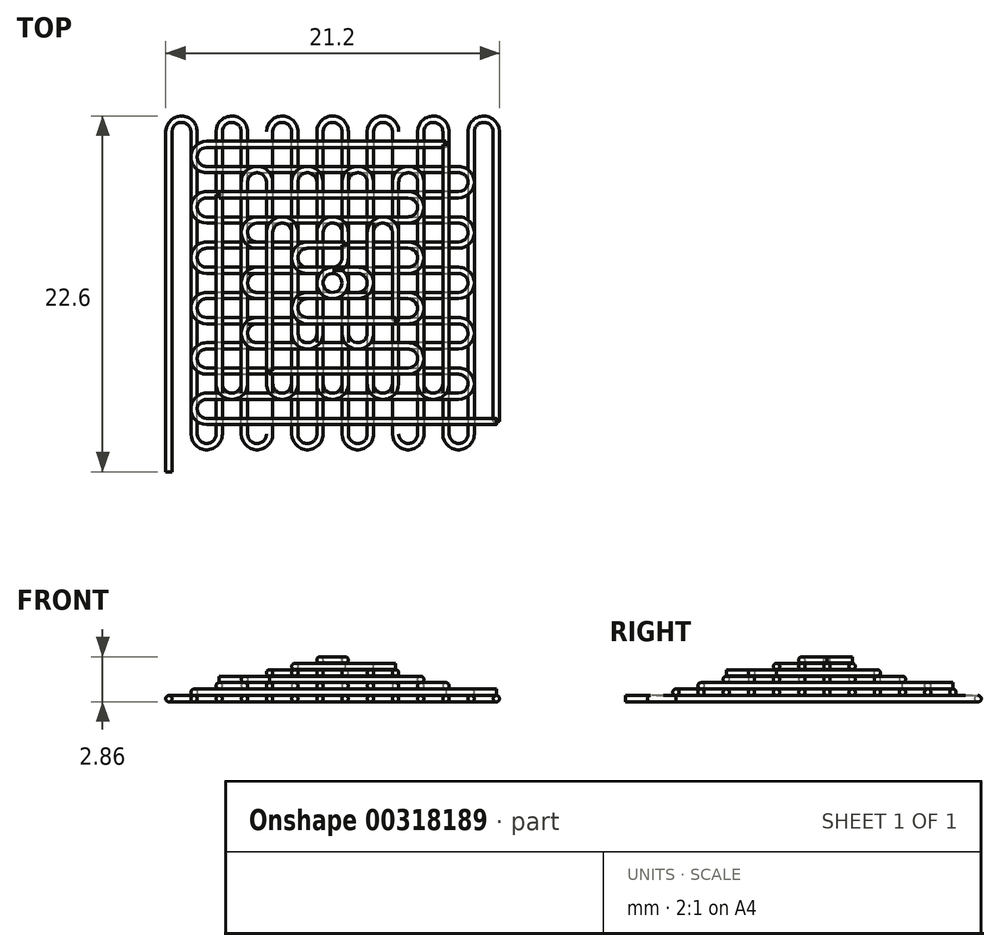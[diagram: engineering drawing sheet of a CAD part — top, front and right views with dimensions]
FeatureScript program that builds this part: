
annotation { "Feature Type Name" : "Feature", "Feature Type Description" : "" }
export const myFeature = defineFeature(function(context is Context, id is Id, definition is map)
    precondition{}
    {
        {
            var Q0;
            Q0=qCreatedBy(makeId("Top.planeOp"),FACE);
            cPlane(context, id + "F0", {"entities" : qUnion([Q0]), "cplaneType" : CPlaneType.OFFSET, "offset" : 0.2 * mm, "width" : 150 * mm, "height" : 150 * mm});
        }
        {
            var Q0;
            Q0=qCreatedBy(id+"F0.planeOp",FACE);
            var sketch = newSketch(context, id + "F1", { "sketchPlane" : qUnion([Q0])});
            skLineSegment(sketch, "E0.bottom", {"start": v(10.4, 10.4) * mm, "end": v(-10.4, 10.4) * mm});
            skLineSegment(sketch, "E0.top", {"start": v(10.4, -10.4) * mm, "end": v(-10.4, -10.4) * mm});
            skLineSegment(sketch, "E0.left", {"start": v(10.4, 10.4) * mm, "end": v(10.4, -10.4) * mm});
            skLineSegment(sketch, "E0.right", {"start": v(-10.4, 9.6) * mm, "end": v(-10.4, -10.4) * mm});
            skPoint(sketch, "E0.middle", {"position": v(0, 0) * mm});
            skLineSegment(sketch, "E1", {"start": v(-9.6, 10.4) * mm, "end": v(-9.6, 10.4) * mm});
            skLineSegment(sketch, "E2", {"start": v(-8.8, 9.6) * mm, "end": v(-8.8, -9.6) * mm});
            skLineSegment(sketch, "E3", {"start": v(-8.8, -10.4) * mm, "end": v(-10.4, -10.4) * mm});
            skLineSegment(sketch, "E4", {"start": v(-8.8, 10.4) * mm, "end": v(-7.2, 10.4) * mm});
            skLineSegment(sketch, "E5", {"start": v(-7.2, 10.4) * mm, "end": v(-7.2, -9.6) * mm});
            skLineSegment(sketch, "E6", {"start": v(-8, -10.4) * mm, "end": v(-8, -10.4) * mm});
            skPoint(sketch, "E7.visualSharp", {"position": v(-10.4, 10.4) * mm});
            skArc(sketch, "E7.filletArc", {"start": v(-9.6, 10.4) * mm, "mid": v(-10.17, 10.17) * mm, "end": v(-10.4, 9.6) * mm});
            skPoint(sketch, "E8.visualSharp", {"position": v(-8.8, 10.4) * mm});
            skArc(sketch, "E8.filletArc", {"start": v(-8.8, 9.6) * mm, "mid": v(-9.03, 10.17) * mm, "end": v(-9.6, 10.4) * mm});
            skPoint(sketch, "E9.visualSharp", {"position": v(-8.8, -10.4) * mm});
            skArc(sketch, "E9.filletArc", {"start": v(-8.8, -9.6) * mm, "mid": v(-8.57, -10.17) * mm, "end": v(-8, -10.4) * mm});
            skPoint(sketch, "E10.visualSharp", {"position": v(-7.2, -10.4) * mm});
            skArc(sketch, "E10.filletArc", {"start": v(-8, -10.4) * mm, "mid": v(-7.43, -10.17) * mm, "end": v(-7.2, -9.6) * mm});
            skLineSegment(sketch, "E11", {"start": v(-7.2, 9.6) * mm, "end": v(-7.2, -9.6) * mm});
            skArc(sketch, "E12.1.0.0", {"start": v(-6.4, 10.4) * mm, "mid": v(-6.97, 10.17) * mm, "end": v(-7.2, 9.6) * mm});
            skArc(sketch, "E12.1.0.1", {"start": v(-5.6, 9.6) * mm, "mid": v(-5.83, 10.17) * mm, "end": v(-6.4, 10.4) * mm});
            skLineSegment(sketch, "E12.1.0.2", {"start": v(-5.6, 9.6) * mm, "end": v(-5.6, -9.6) * mm});
            skArc(sketch, "E12.1.0.3", {"start": v(-5.6, -9.6) * mm, "mid": v(-5.37, -10.17) * mm, "end": v(-4.8, -10.4) * mm});
            skArc(sketch, "E12.1.0.4", {"start": v(-4.8, -10.4) * mm, "mid": v(-4.23, -10.17) * mm, "end": v(-4, -9.6) * mm});
            skLineSegment(sketch, "E12.1.0.5", {"start": v(-4, 9.6) * mm, "end": v(-4, -9.6) * mm});
            skArc(sketch, "E12.2.0.0", {"start": v(-3.2, 10.4) * mm, "mid": v(-3.77, 10.17) * mm, "end": v(-4, 9.6) * mm});
            skArc(sketch, "E12.2.0.1", {"start": v(-2.4, 9.6) * mm, "mid": v(-2.63, 10.17) * mm, "end": v(-3.2, 10.4) * mm});
            skLineSegment(sketch, "E12.2.0.2", {"start": v(-2.4, 9.6) * mm, "end": v(-2.4, -9.6) * mm});
            skArc(sketch, "E12.2.0.3", {"start": v(-2.4, -9.6) * mm, "mid": v(-2.17, -10.17) * mm, "end": v(-1.6, -10.4) * mm});
            skArc(sketch, "E12.2.0.4", {"start": v(-1.6, -10.4) * mm, "mid": v(-1.03, -10.17) * mm, "end": v(-0.8, -9.6) * mm});
            skLineSegment(sketch, "E12.2.0.5", {"start": v(-0.8, 9.6) * mm, "end": v(-0.8, -9.6) * mm});
            skArc(sketch, "E12.3.0.0", {"start": v(0, 10.4) * mm, "mid": v(-0.57, 10.17) * mm, "end": v(-0.8, 9.6) * mm});
            skArc(sketch, "E12.3.0.1", {"start": v(0.8, 9.6) * mm, "mid": v(0.57, 10.17) * mm, "end": v(0, 10.4) * mm});
            skLineSegment(sketch, "E12.3.0.2", {"start": v(0.8, 9.6) * mm, "end": v(0.8, -9.6) * mm});
            skArc(sketch, "E12.3.0.3", {"start": v(0.8, -9.6) * mm, "mid": v(1.03, -10.17) * mm, "end": v(1.6, -10.4) * mm});
            skArc(sketch, "E12.3.0.4", {"start": v(1.6, -10.4) * mm, "mid": v(2.17, -10.17) * mm, "end": v(2.4, -9.6) * mm});
            skLineSegment(sketch, "E12.3.0.5", {"start": v(2.4, 9.6) * mm, "end": v(2.4, -9.6) * mm});
            skArc(sketch, "E12.4.0.0", {"start": v(3.2, 10.4) * mm, "mid": v(2.63, 10.17) * mm, "end": v(2.4, 9.6) * mm});
            skArc(sketch, "E12.4.0.1", {"start": v(4, 9.6) * mm, "mid": v(3.77, 10.17) * mm, "end": v(3.2, 10.4) * mm});
            skLineSegment(sketch, "E12.4.0.2", {"start": v(4, 9.6) * mm, "end": v(4, -9.6) * mm});
            skArc(sketch, "E12.4.0.3", {"start": v(4, -9.6) * mm, "mid": v(4.23, -10.17) * mm, "end": v(4.8, -10.4) * mm});
            skArc(sketch, "E12.4.0.4", {"start": v(4.8, -10.4) * mm, "mid": v(5.37, -10.17) * mm, "end": v(5.6, -9.6) * mm});
            skLineSegment(sketch, "E12.4.0.5", {"start": v(5.6, 9.6) * mm, "end": v(5.6, -9.6) * mm});
            skArc(sketch, "E12.5.0.0", {"start": v(6.4, 10.4) * mm, "mid": v(5.83, 10.17) * mm, "end": v(5.6, 9.6) * mm});
            skArc(sketch, "E12.5.0.1", {"start": v(7.2, 9.6) * mm, "mid": v(6.97, 10.17) * mm, "end": v(6.4, 10.4) * mm});
            skLineSegment(sketch, "E12.5.0.2", {"start": v(7.2, 9.6) * mm, "end": v(7.2, -9.6) * mm});
            skArc(sketch, "E12.5.0.3", {"start": v(7.2, -9.6) * mm, "mid": v(7.43, -10.17) * mm, "end": v(8, -10.4) * mm});
            skArc(sketch, "E12.5.0.4", {"start": v(8, -10.4) * mm, "mid": v(8.57, -10.17) * mm, "end": v(8.8, -9.6) * mm});
            skLineSegment(sketch, "E12.5.0.5", {"start": v(8.8, 9.6) * mm, "end": v(8.8, -9.6) * mm});
            skLineSegment(sketch, "E12.direction1", {"start": v(-8, -10.4) * mm, "end": v(-4.8, -10.4) * mm, "construction": true});
            skLineSegment(sketch, "E13", {"start": v(10.4, 10.4) * mm, "end": v(10.4, 9.6) * mm});
            skArc(sketch, "E14", {"start": v(8.8, 9.6) * mm, "mid": v(9.6, 10.4) * mm, "end": v(10.4, 9.6) * mm});
            skLineSegment(sketch, "E15", {"start": v(-10.4, 9.6) * mm, "end": v(-10.4, -12) * mm});
            skLineSegment(sketch, "E16", {"start": v(10.4, -10.4) * mm, "end": v(10.4, -8.8) * mm});
            skLineSegment(sketch, "E17", {"start": v(10.4, -8.8) * mm, "end": v(10.4, 9.6) * mm});
            skSolve(sketch);
        }
        {
            var Q0;
            Q0=qCreatedBy(id+"F0.planeOp",FACE);
            cPlane(context, id + "F2", {"entities" : qUnion([Q0]), "cplaneType" : CPlaneType.OFFSET, "offset" : 0.4 * mm, "width" : 150 * mm, "height" : 150 * mm});
        }
        {
            var Q0;
            Q0=qCreatedBy(id+"F2.planeOp",FACE);
            var sketch = newSketch(context, id + "F3", { "sketchPlane" : qUnion([Q0])});
            skLineSegment(sketch, "E18.bottom", {"start": v(8.8, 8.8) * mm, "end": v(-8.8, 8.8) * mm});
            skLineSegment(sketch, "E18.top", {"start": v(8.8, -8.8) * mm, "end": v(-8, -8.8) * mm});
            skLineSegment(sketch, "E18.left", {"start": v(8.8, 8.8) * mm, "end": v(8.8, -8.8) * mm});
            skLineSegment(sketch, "E18.right", {"start": v(-8.8, 8.8) * mm, "end": v(-8.8, -8.8) * mm});
            skPoint(sketch, "E18.middle", {"position": v(0, 0) * mm});
            skLineSegment(sketch, "E19", {"start": v(-8.8, -8) * mm, "end": v(-8.8, -8) * mm});
            skLineSegment(sketch, "E20", {"start": v(-8, -7.2) * mm, "end": v(8, -7.2) * mm});
            skLineSegment(sketch, "E21", {"start": v(8.8, -7.2) * mm, "end": v(8.8, -8.8) * mm});
            skLineSegment(sketch, "E22", {"start": v(-8.8, -7.2) * mm, "end": v(-8.8, -5.6) * mm});
            skLineSegment(sketch, "E23", {"start": v(-8.8, -5.6) * mm, "end": v(8, -5.6) * mm});
            skLineSegment(sketch, "E24", {"start": v(8.8, -6.4) * mm, "end": v(8.8, -6.4) * mm});
            skPoint(sketch, "E25.visualSharp", {"position": v(-8.8, -8.8) * mm});
            skArc(sketch, "E25.filletArc", {"start": v(-8.8, -8) * mm, "mid": v(-8.57, -8.57) * mm, "end": v(-8, -8.8) * mm});
            skPoint(sketch, "E26.visualSharp", {"position": v(-8.8, -7.2) * mm});
            skArc(sketch, "E26.filletArc", {"start": v(-8, -7.2) * mm, "mid": v(-8.57, -7.43) * mm, "end": v(-8.8, -8) * mm});
            skPoint(sketch, "E27.visualSharp", {"position": v(8.8, -7.2) * mm});
            skArc(sketch, "E27.filletArc", {"start": v(8, -7.2) * mm, "mid": v(8.57, -6.97) * mm, "end": v(8.8, -6.4) * mm});
            skPoint(sketch, "E28.visualSharp", {"position": v(8.8, -5.6) * mm});
            skArc(sketch, "E28.filletArc", {"start": v(8.8, -6.4) * mm, "mid": v(8.57, -5.83) * mm, "end": v(8, -5.6) * mm});
            skLineSegment(sketch, "E29", {"start": v(-8, -5.6) * mm, "end": v(8, -5.6) * mm});
            skArc(sketch, "E30.1.0.0", {"start": v(-8.8, -4.8) * mm, "mid": v(-8.57, -5.37) * mm, "end": v(-8, -5.6) * mm});
            skArc(sketch, "E30.1.0.1", {"start": v(-8, -4) * mm, "mid": v(-8.57, -4.23) * mm, "end": v(-8.8, -4.8) * mm});
            skLineSegment(sketch, "E30.1.0.2", {"start": v(-8, -4) * mm, "end": v(8, -4) * mm});
            skArc(sketch, "E30.1.0.3", {"start": v(8, -4) * mm, "mid": v(8.57, -3.77) * mm, "end": v(8.8, -3.2) * mm});
            skArc(sketch, "E30.1.0.4", {"start": v(8.8, -3.2) * mm, "mid": v(8.57, -2.63) * mm, "end": v(8, -2.4) * mm});
            skLineSegment(sketch, "E30.1.0.5", {"start": v(-8, -2.4) * mm, "end": v(8, -2.4) * mm});
            skArc(sketch, "E30.2.0.0", {"start": v(-8.8, -1.6) * mm, "mid": v(-8.57, -2.17) * mm, "end": v(-8, -2.4) * mm});
            skArc(sketch, "E30.2.0.1", {"start": v(-8, -0.8) * mm, "mid": v(-8.57, -1.03) * mm, "end": v(-8.8, -1.6) * mm});
            skLineSegment(sketch, "E30.2.0.2", {"start": v(-8, -0.8) * mm, "end": v(8, -0.8) * mm});
            skArc(sketch, "E30.2.0.3", {"start": v(8, -0.8) * mm, "mid": v(8.57, -0.57) * mm, "end": v(8.8, 0) * mm});
            skArc(sketch, "E30.2.0.4", {"start": v(8.8, 0) * mm, "mid": v(8.57, 0.57) * mm, "end": v(8, 0.8) * mm});
            skLineSegment(sketch, "E30.2.0.5", {"start": v(-8, 0.8) * mm, "end": v(8, 0.8) * mm});
            skArc(sketch, "E30.3.0.0", {"start": v(-8.8, 1.6) * mm, "mid": v(-8.57, 1.03) * mm, "end": v(-8, 0.8) * mm});
            skArc(sketch, "E30.3.0.1", {"start": v(-8, 2.4) * mm, "mid": v(-8.57, 2.17) * mm, "end": v(-8.8, 1.6) * mm});
            skLineSegment(sketch, "E30.3.0.2", {"start": v(-8, 2.4) * mm, "end": v(8, 2.4) * mm});
            skArc(sketch, "E30.3.0.3", {"start": v(8, 2.4) * mm, "mid": v(8.57, 2.63) * mm, "end": v(8.8, 3.2) * mm});
            skArc(sketch, "E30.3.0.4", {"start": v(8.8, 3.2) * mm, "mid": v(8.57, 3.77) * mm, "end": v(8, 4) * mm});
            skLineSegment(sketch, "E30.3.0.5", {"start": v(-8, 4) * mm, "end": v(8, 4) * mm});
            skArc(sketch, "E30.4.0.0", {"start": v(-8.8, 4.8) * mm, "mid": v(-8.57, 4.23) * mm, "end": v(-8, 4) * mm});
            skArc(sketch, "E30.4.0.1", {"start": v(-8, 5.6) * mm, "mid": v(-8.57, 5.37) * mm, "end": v(-8.8, 4.8) * mm});
            skLineSegment(sketch, "E30.4.0.2", {"start": v(-8, 5.6) * mm, "end": v(8, 5.6) * mm});
            skArc(sketch, "E30.4.0.3", {"start": v(8, 5.6) * mm, "mid": v(8.57, 5.83) * mm, "end": v(8.8, 6.4) * mm});
            skArc(sketch, "E30.4.0.4", {"start": v(8.8, 6.4) * mm, "mid": v(8.57, 6.97) * mm, "end": v(8, 7.2) * mm});
            skLineSegment(sketch, "E30.4.0.5", {"start": v(-8, 7.2) * mm, "end": v(8, 7.2) * mm});
            skLineSegment(sketch, "E30.direction1", {"start": v(-8, -8.8) * mm, "end": v(-8, -5.6) * mm, "construction": true});
            skLineSegment(sketch, "E31", {"start": v(-8.8, 8.8) * mm, "end": v(-8, 8.8) * mm});
            skArc(sketch, "E32", {"start": v(-8, 7.2) * mm, "mid": v(-8.8, 8) * mm, "end": v(-8, 8.8) * mm});
            skLineSegment(sketch, "E33", {"start": v(8.8, 8.8) * mm, "end": v(7.2, 8.8) * mm});
            skLineSegment(sketch, "E34", {"start": v(-8, -8.8) * mm, "end": v(10.4, -8.8) * mm});
            skLineSegment(sketch, "E35", {"start": v(7.2, 8.8) * mm, "end": v(-8, 8.8) * mm});
            skSolve(sketch);
        }
        {
            var Q0;
            Q0=qCreatedBy(id+"F2.planeOp",FACE);
            cPlane(context, id + "F4", {"entities" : qUnion([Q0]), "cplaneType" : CPlaneType.OFFSET, "offset" : 0.4 * mm, "width" : 150 * mm, "height" : 150 * mm});
        }
        {
            var Q0;
            Q0=qCreatedBy(id+"F4.planeOp",FACE);
            var sketch = newSketch(context, id + "F5", { "sketchPlane" : qUnion([Q0])});
            skLineSegment(sketch, "E36.bottom", {"start": v(4.8, 7.2) * mm, "end": v(4.8, 7.2) * mm});
            skLineSegment(sketch, "E36.top", {"start": v(7.2, -7.2) * mm, "end": v(-7.2, -7.2) * mm});
            skLineSegment(sketch, "E36.left", {"start": v(7.2, 7.2) * mm, "end": v(7.2, -6.4) * mm});
            skPoint(sketch, "E36.middle", {"position": v(0, 0) * mm});
            skLineSegment(sketch, "E37", {"start": v(6.4, -7.2) * mm, "end": v(6.4, -7.2) * mm});
            skLineSegment(sketch, "E38", {"start": v(5.6, -6.4) * mm, "end": v(5.6, 6.4) * mm});
            skLineSegment(sketch, "E39", {"start": v(5.6, -7.2) * mm, "end": v(4, -7.2) * mm});
            skLineSegment(sketch, "E40", {"start": v(4, -7.2) * mm, "end": v(4, 6.4) * mm});
            skPoint(sketch, "E41.visualSharp", {"position": v(7.2, -7.2) * mm});
            skArc(sketch, "E41.filletArc", {"start": v(6.4, -7.2) * mm, "mid": v(6.97, -6.97) * mm, "end": v(7.2, -6.4) * mm});
            skPoint(sketch, "E42.visualSharp", {"position": v(5.6, -7.2) * mm});
            skArc(sketch, "E42.filletArc", {"start": v(5.6, -6.4) * mm, "mid": v(5.83, -6.97) * mm, "end": v(6.4, -7.2) * mm});
            skPoint(sketch, "E43.newPointA", {"position": v(5.6, 7.2) * mm});
            skPoint(sketch, "E43.newPointB", {"position": v(7.2, 7.2) * mm});
            skArc(sketch, "E43.filletArc", {"start": v(5.6, 6.4) * mm, "mid": v(5.37, 6.97) * mm, "end": v(4.8, 7.2) * mm});
            skPoint(sketch, "E44.newPointB", {"position": v(4, 7.2) * mm});
            skArc(sketch, "E44.filletArc", {"start": v(4.8, 7.2) * mm, "mid": v(4.23, 6.97) * mm, "end": v(4, 6.4) * mm});
            skLineSegment(sketch, "E45", {"start": v(4, -6.4) * mm, "end": v(4, 6.4) * mm});
            skArc(sketch, "E46.1.0.0", {"start": v(2.4, -6.4) * mm, "mid": v(2.63, -6.97) * mm, "end": v(3.2, -7.2) * mm});
            skArc(sketch, "E46.1.0.1", {"start": v(3.2, -7.2) * mm, "mid": v(3.77, -6.97) * mm, "end": v(4, -6.4) * mm});
            skLineSegment(sketch, "E46.1.0.2", {"start": v(2.4, -6.4) * mm, "end": v(2.4, 6.4) * mm});
            skArc(sketch, "E46.1.0.3", {"start": v(2.4, 6.4) * mm, "mid": v(2.17, 6.97) * mm, "end": v(1.6, 7.2) * mm});
            skArc(sketch, "E46.1.0.4", {"start": v(1.6, 7.2) * mm, "mid": v(1.03, 6.97) * mm, "end": v(0.8, 6.4) * mm});
            skLineSegment(sketch, "E46.1.0.5", {"start": v(0.8, -6.4) * mm, "end": v(0.8, 6.4) * mm});
            skArc(sketch, "E46.2.0.0", {"start": v(-0.8, -6.4) * mm, "mid": v(-0.57, -6.97) * mm, "end": v(0, -7.2) * mm});
            skArc(sketch, "E46.2.0.1", {"start": v(0, -7.2) * mm, "mid": v(0.57, -6.97) * mm, "end": v(0.8, -6.4) * mm});
            skLineSegment(sketch, "E46.2.0.2", {"start": v(-0.8, -6.4) * mm, "end": v(-0.8, 6.4) * mm});
            skArc(sketch, "E46.2.0.3", {"start": v(-0.8, 6.4) * mm, "mid": v(-1.03, 6.97) * mm, "end": v(-1.6, 7.2) * mm});
            skArc(sketch, "E46.2.0.4", {"start": v(-1.6, 7.2) * mm, "mid": v(-2.17, 6.97) * mm, "end": v(-2.4, 6.4) * mm});
            skLineSegment(sketch, "E46.2.0.5", {"start": v(-2.4, -6.4) * mm, "end": v(-2.4, 6.4) * mm});
            skArc(sketch, "E46.3.0.0", {"start": v(-4, -6.4) * mm, "mid": v(-3.77, -6.97) * mm, "end": v(-3.2, -7.2) * mm});
            skArc(sketch, "E46.3.0.1", {"start": v(-3.2, -7.2) * mm, "mid": v(-2.63, -6.97) * mm, "end": v(-2.4, -6.4) * mm});
            skLineSegment(sketch, "E46.3.0.2", {"start": v(-4, -6.4) * mm, "end": v(-4, 6.4) * mm});
            skArc(sketch, "E46.3.0.3", {"start": v(-4, 6.4) * mm, "mid": v(-4.23, 6.97) * mm, "end": v(-4.8, 7.2) * mm});
            skArc(sketch, "E46.3.0.4", {"start": v(-4.8, 7.2) * mm, "mid": v(-5.37, 6.97) * mm, "end": v(-5.6, 6.4) * mm});
            skLineSegment(sketch, "E46.3.0.5", {"start": v(-5.6, -6.4) * mm, "end": v(-5.6, 6.4) * mm});
            skLineSegment(sketch, "E46.direction1", {"start": v(4, -6.4) * mm, "end": v(0.8, -6.4) * mm, "construction": true});
            skLineSegment(sketch, "E47", {"start": v(-5.6, -6.4) * mm, "end": v(-5.6, -6.4) * mm});
            skLineSegment(sketch, "E48", {"start": v(-6.4, -7.2) * mm, "end": v(-6.4, -7.2) * mm});
            skPoint(sketch, "E49.visualSharp", {"position": v(-5.6, -7.2) * mm});
            skArc(sketch, "E49.filletArc", {"start": v(-6.4, -7.2) * mm, "mid": v(-5.83, -6.97) * mm, "end": v(-5.6, -6.4) * mm});
            skArc(sketch, "E50.filletArc", {"start": v(-7.2, -6.4) * mm, "mid": v(-6.97, -6.97) * mm, "end": v(-6.4, -7.2) * mm});
            skLineSegment(sketch, "E51", {"start": v(-7.2, 7.2) * mm, "end": v(-7.2, 5.6) * mm});
            skLineSegment(sketch, "E52", {"start": v(7.2, -6.4) * mm, "end": v(7.2, 8.8) * mm});
            skLineSegment(sketch, "E53", {"start": v(-7.2, 5.6) * mm, "end": v(-7.2, -6.4) * mm});
            skSolve(sketch);
        }
        {
            var Q0;
            Q0=qCreatedBy(id+"F4.planeOp",FACE);
            cPlane(context, id + "F6", {"entities" : qUnion([Q0]), "cplaneType" : CPlaneType.OFFSET, "offset" : 0.4 * mm, "width" : 150 * mm, "height" : 150 * mm});
        }
        {
            var Q0;
            Q0=qCreatedBy(id+"F6.planeOp",FACE);
            var sketch = newSketch(context, id + "F7", { "sketchPlane" : qUnion([Q0])});
            skLineSegment(sketch, "E54.bottom", {"start": v(4.8, 5.6) * mm, "end": v(-5.6, 5.6) * mm});
            skLineSegment(sketch, "E54.left", {"start": v(5.6, 5.6) * mm, "end": v(5.6, -5.6) * mm});
            skLineSegment(sketch, "E54.right", {"start": v(-5.6, 5.6) * mm, "end": v(-5.6, -5.6) * mm});
            skPoint(sketch, "E54.middle", {"position": v(0, 0) * mm});
            skLineSegment(sketch, "E55", {"start": v(-5.6, 5.6) * mm, "end": v(-5.6, 4) * mm});
            skLineSegment(sketch, "E56", {"start": v(-4.8, 4) * mm, "end": v(4.8, 4) * mm});
            skLineSegment(sketch, "E57", {"start": v(5.6, 4.8) * mm, "end": v(5.6, 4.8) * mm});
            skLineSegment(sketch, "E58", {"start": v(-5.6, 3.2) * mm, "end": v(-5.6, 3.2) * mm});
            skLineSegment(sketch, "E59", {"start": v(-4.8, 2.4) * mm, "end": v(5.6, 2.4) * mm});
            skLineSegment(sketch, "E60", {"start": v(5.6, 2.4) * mm, "end": v(5.6, 4) * mm});
            skPoint(sketch, "E61.visualSharp", {"position": v(5.6, 5.6) * mm});
            skArc(sketch, "E61.filletArc", {"start": v(5.6, 4.8) * mm, "mid": v(5.37, 5.37) * mm, "end": v(4.8, 5.6) * mm});
            skPoint(sketch, "E62.visualSharp", {"position": v(5.6, 4) * mm});
            skArc(sketch, "E62.filletArc", {"start": v(4.8, 4) * mm, "mid": v(5.37, 4.23) * mm, "end": v(5.6, 4.8) * mm});
            skPoint(sketch, "E63.visualSharp", {"position": v(-5.6, 4) * mm});
            skArc(sketch, "E63.filletArc", {"start": v(-4.8, 4) * mm, "mid": v(-5.37, 3.77) * mm, "end": v(-5.6, 3.2) * mm});
            skPoint(sketch, "E64.visualSharp", {"position": v(-5.6, 2.4) * mm});
            skArc(sketch, "E64.filletArc", {"start": v(-5.6, 3.2) * mm, "mid": v(-5.37, 2.63) * mm, "end": v(-4.8, 2.4) * mm});
            skLineSegment(sketch, "E65", {"start": v(4.8, 2.4) * mm, "end": v(-4.8, 2.4) * mm});
            skLineSegment(sketch, "E66", {"start": v(4.8, 5.6) * mm, "end": v(-7.2, 5.6) * mm});
            skArc(sketch, "E67.1.0.0", {"start": v(5.6, 1.6) * mm, "mid": v(5.37, 2.17) * mm, "end": v(4.8, 2.4) * mm});
            skArc(sketch, "E67.1.0.1", {"start": v(4.8, 0.8) * mm, "mid": v(5.37, 1.03) * mm, "end": v(5.6, 1.6) * mm});
            skLineSegment(sketch, "E67.1.0.2", {"start": v(-4.8, 0.8) * mm, "end": v(4.8, 0.8) * mm});
            skArc(sketch, "E67.1.0.3", {"start": v(-4.8, 0.8) * mm, "mid": v(-5.37, 0.57) * mm, "end": v(-5.6, 0) * mm});
            skArc(sketch, "E67.1.0.4", {"start": v(-5.6, 0) * mm, "mid": v(-5.37, -0.57) * mm, "end": v(-4.8, -0.8) * mm});
            skLineSegment(sketch, "E67.1.0.5", {"start": v(4.8, -0.8) * mm, "end": v(-4.8, -0.8) * mm});
            skArc(sketch, "E67.2.0.0", {"start": v(5.6, -1.6) * mm, "mid": v(5.37, -1.03) * mm, "end": v(4.8, -0.8) * mm});
            skArc(sketch, "E67.2.0.1", {"start": v(4.8, -2.4) * mm, "mid": v(5.37, -2.17) * mm, "end": v(5.6, -1.6) * mm});
            skLineSegment(sketch, "E67.2.0.2", {"start": v(-4.8, -2.4) * mm, "end": v(4.8, -2.4) * mm});
            skArc(sketch, "E67.2.0.3", {"start": v(-4.8, -2.4) * mm, "mid": v(-5.37, -2.63) * mm, "end": v(-5.6, -3.2) * mm});
            skArc(sketch, "E67.2.0.4", {"start": v(-5.6, -3.2) * mm, "mid": v(-5.37, -3.77) * mm, "end": v(-4.8, -4) * mm});
            skLineSegment(sketch, "E67.2.0.5", {"start": v(4.8, -4) * mm, "end": v(-4.8, -4) * mm});
            skLineSegment(sketch, "E67.direction1", {"start": v(-4.8, 2.4) * mm, "end": v(-4.8, -0.8) * mm, "construction": true});
            skLineSegment(sketch, "E68", {"start": v(5.6, -5.6) * mm, "end": v(4.8, -5.6) * mm});
            skArc(sketch, "E69", {"start": v(4.8, -4) * mm, "mid": v(5.6, -4.8) * mm, "end": v(4.8, -5.6) * mm});
            skLineSegment(sketch, "E70", {"start": v(-5.6, -5.6) * mm, "end": v(-4, -5.6) * mm});
            skLineSegment(sketch, "E71", {"start": v(-4, -5.6) * mm, "end": v(4.8, -5.6) * mm});
            skSolve(sketch);
        }
        {
            var Q0;
            Q0=qCreatedBy(id+"F6.planeOp",FACE);
            cPlane(context, id + "F8", {"entities" : qUnion([Q0]), "cplaneType" : CPlaneType.OFFSET, "offset" : 0.4 * mm, "width" : 150 * mm, "height" : 150 * mm});
        }
        {
            var Q0;
            Q0=qCreatedBy(id+"F8.planeOp",FACE);
            var sketch = newSketch(context, id + "F9", { "sketchPlane" : qUnion([Q0])});
            skLineSegment(sketch, "E72.bottom", {"start": v(4, 4) * mm, "end": v(-4, 4) * mm});
            skLineSegment(sketch, "E72.top", {"start": v(4, -4) * mm, "end": v(-4, -4) * mm});
            skLineSegment(sketch, "E72.left", {"start": v(4, 4) * mm, "end": v(4, -4) * mm});
            skLineSegment(sketch, "E72.right", {"start": v(-4, 3.2) * mm, "end": v(-4, -4) * mm});
            skPoint(sketch, "E72.middle", {"position": v(0, 0) * mm});
            skLineSegment(sketch, "E73", {"start": v(-3.2, 4) * mm, "end": v(-3.2, 4) * mm});
            skLineSegment(sketch, "E74", {"start": v(-2.4, 3.2) * mm, "end": v(-2.4, -3.2) * mm});
            skLineSegment(sketch, "E75", {"start": v(-2.4, -4) * mm, "end": v(-4, -4) * mm});
            skLineSegment(sketch, "E76", {"start": v(-2.4, 4) * mm, "end": v(-0.8, 4) * mm});
            skLineSegment(sketch, "E77", {"start": v(-0.8, 4) * mm, "end": v(-0.8, -3.2) * mm});
            skLineSegment(sketch, "E78", {"start": v(-1.6, -4) * mm, "end": v(-1.6, -4) * mm});
            skPoint(sketch, "E79.visualSharp", {"position": v(-4, 4) * mm});
            skArc(sketch, "E79.filletArc", {"start": v(-3.2, 4) * mm, "mid": v(-3.77, 3.77) * mm, "end": v(-4, 3.2) * mm});
            skPoint(sketch, "E80.visualSharp", {"position": v(-2.4, 4) * mm});
            skArc(sketch, "E80.filletArc", {"start": v(-2.4, 3.2) * mm, "mid": v(-2.63, 3.77) * mm, "end": v(-3.2, 4) * mm});
            skPoint(sketch, "E81.visualSharp", {"position": v(-2.4, -4) * mm});
            skArc(sketch, "E81.filletArc", {"start": v(-2.4, -3.2) * mm, "mid": v(-2.17, -3.77) * mm, "end": v(-1.6, -4) * mm});
            skPoint(sketch, "E82.visualSharp", {"position": v(-0.8, -4) * mm});
            skArc(sketch, "E82.filletArc", {"start": v(-1.6, -4) * mm, "mid": v(-1.03, -3.77) * mm, "end": v(-0.8, -3.2) * mm});
            skLineSegment(sketch, "E83", {"start": v(-4, 3.2) * mm, "end": v(-4, -5.6) * mm});
            skLineSegment(sketch, "E84", {"start": v(-0.8, 3.2) * mm, "end": v(-0.8, -3.2) * mm});
            skLineSegment(sketch, "E85.1.0.0", {"start": v(2.4, 3.2) * mm, "end": v(2.4, -3.2) * mm});
            skArc(sketch, "E85.1.0.1", {"start": v(1.6, -4) * mm, "mid": v(2.17, -3.77) * mm, "end": v(2.4, -3.2) * mm});
            skArc(sketch, "E85.1.0.2", {"start": v(0.8, -3.2) * mm, "mid": v(1.03, -3.77) * mm, "end": v(1.6, -4) * mm});
            skLineSegment(sketch, "E85.1.0.3", {"start": v(0.8, 3.2) * mm, "end": v(0.8, -3.2) * mm});
            skArc(sketch, "E85.1.0.4", {"start": v(0.8, 3.2) * mm, "mid": v(0.57, 3.77) * mm, "end": v(0, 4) * mm});
            skArc(sketch, "E85.1.0.5", {"start": v(0, 4) * mm, "mid": v(-0.57, 3.77) * mm, "end": v(-0.8, 3.2) * mm});
            skLineSegment(sketch, "E85.direction1", {"start": v(-1.6, -4) * mm, "end": v(1.6, -4) * mm, "construction": true});
            skLineSegment(sketch, "E86", {"start": v(4, -4) * mm, "end": v(4, -2.4) * mm});
            skLineSegment(sketch, "E87", {"start": v(4, 4) * mm, "end": v(4, 3.2) * mm});
            skArc(sketch, "E88", {"start": v(2.4, 3.2) * mm, "mid": v(3.2, 4) * mm, "end": v(4, 3.2) * mm});
            skLineSegment(sketch, "E89", {"start": v(4, -2.4) * mm, "end": v(4, 3.2) * mm});
            skSolve(sketch);
        }
        {
            var Q0;
            Q0=qCreatedBy(id+"F8.planeOp",FACE);
            cPlane(context, id + "F10", {"entities" : qUnion([Q0]), "cplaneType" : CPlaneType.OFFSET, "offset" : 0.4 * mm, "width" : 150 * mm, "height" : 150 * mm});
        }
        {
            var Q0;
            Q0=qCreatedBy(id+"F10.planeOp",FACE);
            var sketch = newSketch(context, id + "F11", { "sketchPlane" : qUnion([Q0])});
            skLineSegment(sketch, "E90.top", {"start": v(2.4, -2.4) * mm, "end": v(-1.6, -2.4) * mm});
            skLineSegment(sketch, "E90.left", {"start": v(2.4, 0) * mm, "end": v(2.4, 0) * mm});
            skLineSegment(sketch, "E90.right", {"start": v(-2.4, 1.6) * mm, "end": v(-2.4, 1.6) * mm});
            skPoint(sketch, "E90.middle", {"position": v(0, 0) * mm});
            skLineSegment(sketch, "E91", {"start": v(-2.4, -1.6) * mm, "end": v(-2.4, -1.6) * mm});
            skLineSegment(sketch, "E92", {"start": v(-1.6, -0.8) * mm, "end": v(1.6, -0.8) * mm});
            skLineSegment(sketch, "E93", {"start": v(1.6, 0.8) * mm, "end": v(-1.6, 0.8) * mm});
            skPoint(sketch, "E94.visualSharp", {"position": v(-2.4, -2.4) * mm});
            skArc(sketch, "E94.filletArc", {"start": v(-2.4, -1.6) * mm, "mid": v(-2.17, -2.17) * mm, "end": v(-1.6, -2.4) * mm});
            skPoint(sketch, "E95.visualSharp", {"position": v(-2.4, -0.8) * mm});
            skArc(sketch, "E95.filletArc", {"start": v(-1.6, -0.8) * mm, "mid": v(-2.17, -1.03) * mm, "end": v(-2.4, -1.6) * mm});
            skArc(sketch, "E96.filletArc", {"start": v(1.6, -0.8) * mm, "mid": v(2.17, -0.57) * mm, "end": v(2.4, 0) * mm});
            skArc(sketch, "E97.filletArc", {"start": v(2.4, 0) * mm, "mid": v(2.17, 0.57) * mm, "end": v(1.6, 0.8) * mm});
            skArc(sketch, "E98.filletArc", {"start": v(-2.4, 1.6) * mm, "mid": v(-2.17, 1.03) * mm, "end": v(-1.6, 0.8) * mm});
            skPoint(sketch, "E99.visualSharp", {"position": v(-2.4, 2.4) * mm});
            skArc(sketch, "E99.filletArc", {"start": v(-1.6, 2.4) * mm, "mid": v(-2.17, 2.17) * mm, "end": v(-2.4, 1.6) * mm});
            skLineSegment(sketch, "E100", {"start": v(-1.6, -2.4) * mm, "end": v(4, -2.4) * mm});
            skLineSegment(sketch, "E101", {"start": v(2.4, 2.4) * mm, "end": v(0.8, 2.4) * mm});
            skLineSegment(sketch, "E102", {"start": v(0.8, 2.4) * mm, "end": v(-1.6, 2.4) * mm});
            skSolve(sketch);
        }
        {
            var Q0;
            Q0=qCreatedBy(id+"F10.planeOp",FACE);
            cPlane(context, id + "F12", {"entities" : qUnion([Q0]), "cplaneType" : CPlaneType.OFFSET, "offset" : 0.4 * mm, "width" : 150 * mm, "height" : 150 * mm});
        }
        {
            var Q0;
            Q0=qCreatedBy(id+"F12.planeOp",FACE);
            var sketch = newSketch(context, id + "F13", { "sketchPlane" : qUnion([Q0])});
            skCircle(sketch, "E103", {"center": v(0, 0) * mm, "radius": 0.8 * mm});
            skLineSegment(sketch, "E104", {"start": v(0, 0) * mm, "end": v(0, 0.8) * mm});
            skLineSegment(sketch, "E105", {"start": v(0, 0.8) * mm, "end": v(0, 0.8) * mm});
            skLineSegment(sketch, "E106", {"start": v(0.8, 1.6) * mm, "end": v(0.8, 2.4) * mm});
            skPoint(sketch, "E107.visualSharp", {"position": v(0.8, 0.8) * mm});
            skArc(sketch, "E107.filletArc", {"start": v(0, 0.8) * mm, "mid": v(0.57, 1.03) * mm, "end": v(0.8, 1.6) * mm});
            skLineSegment(sketch, "E108", {"start": v(0, 0) * mm, "end": v(0, -0.8) * mm});
            skArc(sketch, "E109", {"start": v(0, -0.8) * mm, "mid": v(-0.8, 0) * mm, "end": v(0, 0.8) * mm});
            skArc(sketch, "E110", {"start": v(0, -0.8) * mm, "mid": v(0.8, 0) * mm, "end": v(0, 0.8) * mm});
            skSolve(sketch);
        }
        {
            var Q0;
            Q0=sQuery(id+"F1.wireOp",EDGE,"E17");
            var Q1;
            Q1=sQuery(id+"F1.wireOp",VERTEX,"E17.start");
            cPlane(context, id + "F14", {"entities" : qUnion([Q0, Q1]), "cplaneType" : CPlaneType.LINE_POINT, "offset" : 25 * mm, "width" : 150 * mm, "height" : 150 * mm});
        }
        {
            var Q0;
            Q0=qCreatedBy(id+"F14.planeOp",FACE);
            var sketch = newSketch(context, id + "F15", { "sketchPlane" : qUnion([Q0])});
            skCircle(sketch, "E111", {"center": v(-10.4, 0.21) * mm, "radius": 0.2 * mm});
            skSolve(sketch);
        }
        {
            var Q0;
            Q0=makeQuery(id+"F15.imprint","IMPRINT",FACE,{"disambiguationData":[TD([[makeQuery(id+"F15.imprint","IMPRINT",EDGE,{"derivedFrom":sQuery(id+"F15.wireOp",EDGE,"E111")}),1.0]])]});
            var Q1;
            Q1=sQuery(id+"F1.wireOp",EDGE,"E17");
            var Q2;
            Q2=sQuery(id+"F1.wireOp",EDGE,"E14");
            var Q3;
            Q3=sQuery(id+"F1.wireOp",EDGE,"E12.5.0.5");
            var Q4;
            Q4=sQuery(id+"F1.wireOp",EDGE,"E12.5.0.4");
            var Q5;
            Q5=sQuery(id+"F1.wireOp",EDGE,"E12.5.0.2");
            var Q6;
            Q6=sQuery(id+"F1.wireOp",EDGE,"E12.5.0.3");
            var Q7;
            Q7=sQuery(id+"F1.wireOp",EDGE,"E12.5.0.1");
            var Q8;
            Q8=sQuery(id+"F1.wireOp",EDGE,"E12.5.0.0");
            var Q9;
            Q9=sQuery(id+"F1.wireOp",EDGE,"E12.4.0.5");
            var Q10;
            Q10=sQuery(id+"F1.wireOp",EDGE,"E12.4.0.2");
            var Q11;
            Q11=sQuery(id+"F1.wireOp",EDGE,"E12.4.0.1");
            var Q12;
            Q12=sQuery(id+"F1.wireOp",EDGE,"E12.4.0.0");
            var Q13;
            Q13=sQuery(id+"F1.wireOp",EDGE,"E12.3.0.5");
            var Q14;
            Q14=sQuery(id+"F1.wireOp",EDGE,"E12.4.0.4");
            var Q15;
            Q15=sQuery(id+"F1.wireOp",EDGE,"E12.4.0.3");
            var Q16;
            Q16=sQuery(id+"F1.wireOp",EDGE,"E12.3.0.4");
            var Q17;
            Q17=sQuery(id+"F1.wireOp",EDGE,"E12.3.0.3");
            var Q18;
            Q18=sQuery(id+"F1.wireOp",EDGE,"E12.3.0.2");
            var Q19;
            Q19=sQuery(id+"F1.wireOp",EDGE,"E12.3.0.0");
            var Q20;
            Q20=sQuery(id+"F1.wireOp",EDGE,"E12.3.0.1");
            var Q21;
            Q21=sQuery(id+"F1.wireOp",EDGE,"E12.2.0.5");
            var Q22;
            Q22=sQuery(id+"F1.wireOp",EDGE,"E12.2.0.4");
            var Q23;
            Q23=sQuery(id+"F1.wireOp",EDGE,"E12.2.0.3");
            var Q24;
            Q24=sQuery(id+"F1.wireOp",EDGE,"E12.2.0.2");
            var Q25;
            Q25=sQuery(id+"F1.wireOp",EDGE,"E12.2.0.1");
            var Q26;
            Q26=sQuery(id+"F1.wireOp",EDGE,"E12.2.0.0");
            var Q27;
            Q27=sQuery(id+"F1.wireOp",EDGE,"E12.1.0.5");
            var Q28;
            Q28=sQuery(id+"F1.wireOp",EDGE,"E12.1.0.4");
            var Q29;
            Q29=sQuery(id+"F1.wireOp",EDGE,"E12.1.0.3");
            var Q30;
            Q30=sQuery(id+"F1.wireOp",EDGE,"E12.1.0.2");
            var Q31;
            Q31=sQuery(id+"F1.wireOp",EDGE,"E12.1.0.1");
            var Q32;
            Q32=sQuery(id+"F1.wireOp",EDGE,"E12.1.0.0");
            var Q33;
            Q33=sQuery(id+"F1.wireOp",EDGE,"E11");
            var Q34;
            Q34=sQuery(id+"F1.wireOp",EDGE,"E10.filletArc");
            var Q35;
            Q35=sQuery(id+"F1.wireOp",EDGE,"E9.filletArc");
            var Q36;
            Q36=sQuery(id+"F1.wireOp",EDGE,"E2");
            var Q37;
            Q37=sQuery(id+"F1.wireOp",EDGE,"E8.filletArc");
            var Q38;
            Q38=sQuery(id+"F1.wireOp",EDGE,"E7.filletArc");
            var Q39;
            Q39=sQuery(id+"F1.wireOp",EDGE,"E15");
            sweep(context, id + "F16", {"profiles" : qUnion([Q0]), "path" : qUnion([Q1, Q2, Q3, Q4, Q5, Q6, Q7, Q8, Q9, Q10, Q11, Q12, Q13, Q14, Q15, Q16, Q17, Q18, Q19, Q20, Q21, Q22, Q23, Q24, Q25, Q26, Q27, Q28, Q29, Q30, Q31, Q32, Q33, Q34, Q35, Q36, Q37, Q38, Q39])});
        }
        {
            var Q0;
            Q0=sQuery(id+"F3.wireOp",VERTEX,"E35.start");
            var Q1;
            Q1=sQuery(id+"F3.wireOp",EDGE,"E35");
            cPlane(context, id + "F17", {"entities" : qUnion([Q0, Q1]), "cplaneType" : CPlaneType.LINE_POINT, "offset" : 25 * mm, "width" : 150 * mm, "height" : 150 * mm});
        }
        {
            var Q0;
            Q0=qCreatedBy(id+"F17.planeOp",FACE);
            var sketch = newSketch(context, id + "F18", { "sketchPlane" : qUnion([Q0])});
            skCircle(sketch, "E112", {"center": v(-8.8, 0.62) * mm, "radius": 0.2 * mm});
            skSolve(sketch);
        }
        {
            var Q0;
            Q0=makeQuery(id+"F18.imprint","IMPRINT",FACE,{"disambiguationData":[TD([[makeQuery(id+"F18.imprint","IMPRINT",EDGE,{"derivedFrom":sQuery(id+"F18.wireOp",EDGE,"E112")}),1.0]])]});
            var Q1;
            Q1=sQuery(id+"F3.wireOp",EDGE,"E35");
            var Q2;
            Q2=sQuery(id+"F3.wireOp",EDGE,"E32");
            var Q3;
            Q3=sQuery(id+"F3.wireOp",EDGE,"E30.4.0.5");
            var Q4;
            Q4=sQuery(id+"F3.wireOp",EDGE,"E30.4.0.4");
            var Q5;
            Q5=sQuery(id+"F3.wireOp",EDGE,"E30.4.0.3");
            var Q6;
            Q6=sQuery(id+"F3.wireOp",EDGE,"E30.4.0.2");
            var Q7;
            Q7=sQuery(id+"F3.wireOp",EDGE,"E30.4.0.1");
            var Q8;
            Q8=sQuery(id+"F3.wireOp",EDGE,"E30.4.0.0");
            var Q9;
            Q9=sQuery(id+"F3.wireOp",EDGE,"E30.3.0.5");
            var Q10;
            Q10=sQuery(id+"F3.wireOp",EDGE,"E30.3.0.4");
            var Q11;
            Q11=sQuery(id+"F3.wireOp",EDGE,"E30.3.0.3");
            var Q12;
            Q12=sQuery(id+"F3.wireOp",EDGE,"E30.3.0.2");
            var Q13;
            Q13=sQuery(id+"F3.wireOp",EDGE,"E30.3.0.1");
            var Q14;
            Q14=sQuery(id+"F3.wireOp",EDGE,"E30.3.0.0");
            var Q15;
            Q15=sQuery(id+"F3.wireOp",EDGE,"E30.2.0.5");
            var Q16;
            Q16=sQuery(id+"F3.wireOp",EDGE,"E30.2.0.4");
            var Q17;
            Q17=sQuery(id+"F3.wireOp",EDGE,"E30.2.0.3");
            var Q18;
            Q18=sQuery(id+"F3.wireOp",EDGE,"E30.2.0.2");
            var Q19;
            Q19=sQuery(id+"F3.wireOp",EDGE,"E30.2.0.1");
            var Q20;
            Q20=sQuery(id+"F3.wireOp",EDGE,"E30.2.0.0");
            var Q21;
            Q21=sQuery(id+"F3.wireOp",EDGE,"E30.1.0.5");
            var Q22;
            Q22=sQuery(id+"F3.wireOp",EDGE,"E30.1.0.4");
            var Q23;
            Q23=sQuery(id+"F3.wireOp",EDGE,"E30.1.0.3");
            var Q24;
            Q24=sQuery(id+"F3.wireOp",EDGE,"E30.1.0.2");
            var Q25;
            Q25=sQuery(id+"F3.wireOp",EDGE,"E30.1.0.1");
            var Q26;
            Q26=sQuery(id+"F3.wireOp",EDGE,"E30.1.0.0");
            var Q27;
            Q27=sQuery(id+"F3.wireOp",EDGE,"E29");
            var Q28;
            Q28=sQuery(id+"F3.wireOp",EDGE,"E28.filletArc");
            var Q29;
            Q29=sQuery(id+"F3.wireOp",EDGE,"E27.filletArc");
            var Q30;
            Q30=sQuery(id+"F3.wireOp",EDGE,"E20");
            var Q31;
            Q31=sQuery(id+"F3.wireOp",EDGE,"E26.filletArc");
            var Q32;
            Q32=sQuery(id+"F3.wireOp",EDGE,"E25.filletArc");
            var Q33;
            Q33=sQuery(id+"F3.wireOp",EDGE,"E34");
            sweep(context, id + "F19", {"profiles" : qUnion([Q0]), "path" : qUnion([Q1, Q2, Q3, Q4, Q5, Q6, Q7, Q8, Q9, Q10, Q11, Q12, Q13, Q14, Q15, Q16, Q17, Q18, Q19, Q20, Q21, Q22, Q23, Q24, Q25, Q26, Q27, Q28, Q29, Q30, Q31, Q32, Q33])});
        }
        {
            var Q0;
            Q0=sQuery(id+"F5.wireOp",VERTEX,"E51.end");
            var Q1;
            Q1=sQuery(id+"F5.wireOp",EDGE,"E53");
            cPlane(context, id + "F20", {"entities" : qUnion([Q0, Q1]), "cplaneType" : CPlaneType.LINE_POINT, "offset" : 25 * mm, "width" : 150 * mm, "height" : 150 * mm});
        }
        {
            var Q0;
            Q0=qCreatedBy(id+"F20.planeOp",FACE);
            var sketch = newSketch(context, id + "F21", { "sketchPlane" : qUnion([Q0])});
            skCircle(sketch, "E113", {"center": v(-7.2, 1.03) * mm, "radius": 0.2 * mm});
            skSolve(sketch);
        }
        {
            var Q0;
            Q0=makeQuery(id+"F21.imprint","IMPRINT",FACE,{"disambiguationData":[TD([[makeQuery(id+"F21.imprint","IMPRINT",EDGE,{"derivedFrom":sQuery(id+"F21.wireOp",EDGE,"E113")}),1.0]])]});
            var Q1;
            Q1=sQuery(id+"F5.wireOp",EDGE,"E53");
            var Q2;
            Q2=sQuery(id+"F5.wireOp",EDGE,"E50.filletArc");
            var Q3;
            Q3=sQuery(id+"F5.wireOp",EDGE,"E49.filletArc");
            var Q4;
            Q4=sQuery(id+"F5.wireOp",EDGE,"E46.3.0.5");
            var Q5;
            Q5=sQuery(id+"F5.wireOp",EDGE,"E46.3.0.4");
            var Q6;
            Q6=sQuery(id+"F5.wireOp",EDGE,"E46.3.0.3");
            var Q7;
            Q7=sQuery(id+"F5.wireOp",EDGE,"E46.3.0.2");
            var Q8;
            Q8=sQuery(id+"F5.wireOp",EDGE,"E46.3.0.0");
            var Q9;
            Q9=sQuery(id+"F5.wireOp",EDGE,"E46.3.0.1");
            var Q10;
            Q10=sQuery(id+"F5.wireOp",EDGE,"E46.2.0.5");
            var Q11;
            Q11=sQuery(id+"F5.wireOp",EDGE,"E46.2.0.4");
            var Q12;
            Q12=sQuery(id+"F5.wireOp",EDGE,"E46.2.0.3");
            var Q13;
            Q13=sQuery(id+"F5.wireOp",EDGE,"E46.2.0.2");
            var Q14;
            Q14=sQuery(id+"F5.wireOp",EDGE,"E46.2.0.0");
            var Q15;
            Q15=sQuery(id+"F5.wireOp",EDGE,"E46.2.0.1");
            var Q16;
            Q16=sQuery(id+"F5.wireOp",EDGE,"E46.1.0.5");
            var Q17;
            Q17=sQuery(id+"F5.wireOp",EDGE,"E46.1.0.4");
            var Q18;
            Q18=sQuery(id+"F5.wireOp",EDGE,"E46.1.0.3");
            var Q19;
            Q19=sQuery(id+"F5.wireOp",EDGE,"E46.1.0.2");
            var Q20;
            Q20=sQuery(id+"F5.wireOp",EDGE,"E46.1.0.0");
            var Q21;
            Q21=sQuery(id+"F5.wireOp",EDGE,"E46.1.0.1");
            var Q22;
            Q22=sQuery(id+"F5.wireOp",EDGE,"E45");
            var Q23;
            Q23=sQuery(id+"F5.wireOp",EDGE,"E44.filletArc");
            var Q24;
            Q24=sQuery(id+"F5.wireOp",EDGE,"E43.filletArc");
            var Q25;
            Q25=sQuery(id+"F5.wireOp",EDGE,"E38");
            var Q26;
            Q26=sQuery(id+"F5.wireOp",EDGE,"E42.filletArc");
            var Q27;
            Q27=sQuery(id+"F5.wireOp",EDGE,"E41.filletArc");
            var Q28;
            Q28=sQuery(id+"F5.wireOp",EDGE,"E42.filletArc");
            var Q29;
            Q29=sQuery(id+"F5.wireOp",EDGE,"E52");
            sweep(context, id + "F22", {"profiles" : qUnion([Q0]), "path" : qUnion([Q1, Q2, Q3, Q4, Q5, Q6, Q7, Q8, Q9, Q10, Q11, Q12, Q13, Q14, Q15, Q16, Q17, Q18, Q19, Q20, Q21, Q22, Q23, Q24, Q25, Q26, Q27, Q28, Q29])});
        }
        {
            var Q0;
            Q0=sQuery(id+"F7.wireOp",EDGE,"E71");
            var Q1;
            Q1=sQuery(id+"F7.wireOp",VERTEX,"E71.start");
            cPlane(context, id + "F23", {"entities" : qUnion([Q0, Q1]), "cplaneType" : CPlaneType.LINE_POINT, "offset" : 25 * mm, "width" : 150 * mm, "height" : 150 * mm});
        }
        {
            var Q0;
            Q0=qCreatedBy(id+"F23.planeOp",FACE);
            var sketch = newSketch(context, id + "F24", { "sketchPlane" : qUnion([Q0])});
            skCircle(sketch, "E114", {"center": v(-5.6, 1.44) * mm, "radius": 0.2 * mm});
            skSolve(sketch);
        }
        {
            var Q0;
            Q0=makeQuery(id+"F24.imprint","IMPRINT",FACE,{"disambiguationData":[TD([[makeQuery(id+"F24.imprint","IMPRINT",EDGE,{"derivedFrom":sQuery(id+"F24.wireOp",EDGE,"E114")}),1.0]])]});
            var Q1;
            Q1=sQuery(id+"F7.wireOp",EDGE,"E71");
            var Q2;
            Q2=sQuery(id+"F7.wireOp",EDGE,"E69");
            var Q3;
            Q3=sQuery(id+"F7.wireOp",EDGE,"E67.2.0.5");
            var Q4;
            Q4=sQuery(id+"F7.wireOp",EDGE,"E67.2.0.4");
            var Q5;
            Q5=sQuery(id+"F7.wireOp",EDGE,"E67.2.0.3");
            var Q6;
            Q6=sQuery(id+"F7.wireOp",EDGE,"E67.2.0.2");
            var Q7;
            Q7=sQuery(id+"F7.wireOp",EDGE,"E67.2.0.1");
            var Q8;
            Q8=sQuery(id+"F7.wireOp",EDGE,"E67.2.0.0");
            var Q9;
            Q9=sQuery(id+"F7.wireOp",EDGE,"E67.1.0.5");
            var Q10;
            Q10=sQuery(id+"F7.wireOp",EDGE,"E67.1.0.4");
            var Q11;
            Q11=sQuery(id+"F7.wireOp",EDGE,"E67.1.0.3");
            var Q12;
            Q12=sQuery(id+"F7.wireOp",EDGE,"E67.1.0.2");
            var Q13;
            Q13=sQuery(id+"F7.wireOp",EDGE,"E67.1.0.1");
            var Q14;
            Q14=sQuery(id+"F7.wireOp",EDGE,"E67.1.0.0");
            var Q15;
            Q15=sQuery(id+"F7.wireOp",EDGE,"E65");
            var Q16;
            Q16=sQuery(id+"F7.wireOp",EDGE,"E64.filletArc");
            var Q17;
            Q17=sQuery(id+"F7.wireOp",EDGE,"E63.filletArc");
            var Q18;
            Q18=sQuery(id+"F7.wireOp",EDGE,"E56");
            var Q19;
            Q19=sQuery(id+"F7.wireOp",EDGE,"E62.filletArc");
            var Q20;
            Q20=sQuery(id+"F7.wireOp",EDGE,"E61.filletArc");
            var Q21;
            Q21=sQuery(id+"F7.wireOp",EDGE,"E66");
            sweep(context, id + "F25", {"profiles" : qUnion([Q0]), "path" : qUnion([Q1, Q2, Q3, Q4, Q5, Q6, Q7, Q8, Q9, Q10, Q11, Q12, Q13, Q14, Q15, Q16, Q17, Q18, Q19, Q20, Q21])});
        }
        {
            var Q0;
            Q0=sQuery(id+"F9.wireOp",VERTEX,"E86.end");
            var Q1;
            Q1=sQuery(id+"F9.wireOp",EDGE,"E89");
            cPlane(context, id + "F26", {"entities" : qUnion([Q0, Q1]), "cplaneType" : CPlaneType.LINE_POINT, "offset" : 25 * mm, "width" : 150 * mm, "height" : 150 * mm});
        }
        {
            var Q0;
            Q0=qCreatedBy(id+"F26.planeOp",FACE);
            var sketch = newSketch(context, id + "F27", { "sketchPlane" : qUnion([Q0])});
            skCircle(sketch, "E115", {"center": v(-4, 1.85) * mm, "radius": 0.2 * mm});
            skSolve(sketch);
        }
        {
            var Q0;
            Q0=makeQuery(id+"F27.imprint","IMPRINT",FACE,{"disambiguationData":[TD([[makeQuery(id+"F27.imprint","IMPRINT",EDGE,{"derivedFrom":sQuery(id+"F27.wireOp",EDGE,"E115")}),1.0]])]});
            var Q1;
            Q1=sQuery(id+"F9.wireOp",EDGE,"E89");
            var Q2;
            Q2=sQuery(id+"F9.wireOp",EDGE,"E88");
            var Q3;
            Q3=sQuery(id+"F9.wireOp",EDGE,"E85.1.0.0");
            var Q4;
            Q4=sQuery(id+"F9.wireOp",EDGE,"E85.1.0.1");
            var Q5;
            Q5=sQuery(id+"F9.wireOp",EDGE,"E85.1.0.2");
            var Q6;
            Q6=sQuery(id+"F9.wireOp",EDGE,"E85.1.0.3");
            var Q7;
            Q7=sQuery(id+"F9.wireOp",EDGE,"E85.1.0.4");
            var Q8;
            Q8=sQuery(id+"F9.wireOp",EDGE,"E85.1.0.5");
            var Q9;
            Q9=sQuery(id+"F9.wireOp",EDGE,"E82.filletArc");
            var Q10;
            Q10=sQuery(id+"F9.wireOp",EDGE,"E84");
            var Q11;
            Q11=sQuery(id+"F9.wireOp",EDGE,"E81.filletArc");
            var Q12;
            Q12=sQuery(id+"F9.wireOp",EDGE,"E74");
            var Q13;
            Q13=sQuery(id+"F9.wireOp",EDGE,"E80.filletArc");
            var Q14;
            Q14=sQuery(id+"F9.wireOp",EDGE,"E79.filletArc");
            var Q15;
            Q15=sQuery(id+"F9.wireOp",EDGE,"E83");
            sweep(context, id + "F28", {"profiles" : qUnion([Q0]), "path" : qUnion([Q1, Q2, Q3, Q4, Q5, Q6, Q7, Q8, Q9, Q10, Q11, Q12, Q13, Q14, Q15])});
        }
        {
            var Q0;
            Q0=sQuery(id+"F11.wireOp",VERTEX,"E102.start");
            var Q1;
            Q1=sQuery(id+"F11.wireOp",EDGE,"E102");
            cPlane(context, id + "F29", {"entities" : qUnion([Q0, Q1]), "cplaneType" : CPlaneType.LINE_POINT, "offset" : 25 * mm, "width" : 150 * mm, "height" : 150 * mm});
        }
        {
            var Q0;
            Q0=qCreatedBy(id+"F29.planeOp",FACE);
            var sketch = newSketch(context, id + "F30", { "sketchPlane" : qUnion([Q0])});
            skCircle(sketch, "E116", {"center": v(-2.4, 2.26) * mm, "radius": 0.2 * mm});
            skSolve(sketch);
        }
        {
            var Q0;
            Q0=makeQuery(id+"F30.imprint","IMPRINT",FACE,{"disambiguationData":[TD([[makeQuery(id+"F30.imprint","IMPRINT",EDGE,{"derivedFrom":sQuery(id+"F30.wireOp",EDGE,"E116")}),1.0]])]});
            var Q1;
            Q1=sQuery(id+"F11.wireOp",EDGE,"E102");
            var Q2;
            Q2=sQuery(id+"F11.wireOp",EDGE,"E99.filletArc");
            var Q3;
            Q3=sQuery(id+"F11.wireOp",EDGE,"E98.filletArc");
            var Q4;
            Q4=sQuery(id+"F11.wireOp",EDGE,"E93");
            var Q5;
            Q5=sQuery(id+"F11.wireOp",EDGE,"E97.filletArc");
            var Q6;
            Q6=sQuery(id+"F11.wireOp",EDGE,"E96.filletArc");
            var Q7;
            Q7=sQuery(id+"F11.wireOp",EDGE,"E92");
            var Q8;
            Q8=sQuery(id+"F11.wireOp",EDGE,"E95.filletArc");
            var Q9;
            Q9=sQuery(id+"F11.wireOp",EDGE,"E94.filletArc");
            var Q10;
            Q10=sQuery(id+"F11.wireOp",EDGE,"E100");
            sweep(context, id + "F31", {"profiles" : qUnion([Q0]), "path" : qUnion([Q1, Q2, Q3, Q4, Q5, Q6, Q7, Q8, Q9, Q10])});
        }
        {
            var Q0;
            Q0=sQuery(id+"F13.wireOp",VERTEX,"E108.end");
            var Q1;
            Q1=sQuery(id+"F13.wireOp",EDGE,"E103");
            cPlane(context, id + "F32", {"entities" : qUnion([Q0, Q1]), "cplaneType" : CPlaneType.CURVE_POINT, "offset" : 25 * mm, "width" : 150 * mm, "height" : 150 * mm});
        }
        {
            var Q0;
            Q0=qCreatedBy(id+"F32.planeOp",FACE);
            var sketch = newSketch(context, id + "F33", { "sketchPlane" : qUnion([Q0])});
            skCircle(sketch, "E117", {"center": v(-0.8, 2.67) * mm, "radius": 0.2 * mm});
            skSolve(sketch);
        }
        {
            var Q0;
            Q0=makeQuery(id+"F33.imprint","IMPRINT",FACE,{"disambiguationData":[TD([[makeQuery(id+"F33.imprint","IMPRINT",EDGE,{"derivedFrom":sQuery(id+"F33.wireOp",EDGE,"E117")}),1.0]])]});
            var Q1;
            Q1=sQuery(id+"F13.wireOp",EDGE,"E109");
            var Q2;
            Q2=sQuery(id+"F13.wireOp",EDGE,"E107.filletArc");
            var Q3;
            Q3=sQuery(id+"F13.wireOp",EDGE,"E106");
            sweep(context, id + "F34", {"profiles" : qUnion([Q0]), "path" : qUnion([Q1, Q2, Q3])});
        }
        {
            var Q0;
            Q0=makeQuery(id+"F34.opSweep","CAP_FACE",FACE,{"disambiguationData":[OSD([sQuery(id+"F13.wireOp",VERTEX,"E109.start"),sQuery(id+"F33.wireOp",EDGE,"E117")])],"isStart":true});
            var Q1;
            Q1=sQuery(id+"F13.wireOp",EDGE,"E110");
            sweep(context, id + "F35", {"operationType" : NewBodyOperationType.ADD, "profiles" : qUnion([Q0]), "path" : qUnion([Q1])});
        }
    });
